# Revit family: WALL SQUARE 6W ASIMETRICA_LKC0635A_WW
name_source: partatom
category: Luminarias
units: mm (PartAtom-declared; Revit-internal decimal feet)

## family parameters
Compartido = No
Corte con vacíos al cargar = No
Cota de conector redondo = Diámetro de uso
Origen de luz = Sí
Punto de cálculo de habitación = No
Se basa en plano de trabajo = Sí
Siempre vertical = No
Tipo de pieza = Normal

## types (2) — shared parameters
Ancho = 160 mm  [stored 0.524934 ft]
Cambio de temperatura de color de luz atenuada = <Ninguno>
Comentarios de vataje = 100-240V
Fabricante = BRILLANT
Filtro de color = 16777215
Longitud de símbolo de origen de luz = 500 mm  [stored 1.64042 ft]
Lámpara = OSRAM
Watt per fixture = 6
Ángulo de campo de foco = 45.00°
Ángulo de enfoque = 35.00°
Ángulo de inclinación = 105.00°
zero-valued in all types: Elevación por defecto

## per-type parameters (varying)
| type | Descripción | Modelo |
| EMP_LKC0635A | LUMINARIA TIPO CUADRADO PARA EMPOTRAR EN PISO CON CUERPO DE ALUMINIO FUNDIDO A PRESION, CUBIERTO CON POLVO GRIS OSCURO CON CUBIERTA DE ACERO INOXIDABLE Y VIDRIO TEMPLADO DE 8MM, HOUSING DE METAL 1.5MM CUBIERTO DE POLVO GRIS OSCURO DE 160MM Y 118MM DE PROFUNDO CON PESO DE 2.5KG. CUENTA CON 6 LED TIPO OSRAM CON UNA POTENCIA TOTAL DE 6W, TEMPERATURA EN BLANCO ULTRA CALIDO EN 2000K CON 247 LUMENES, IP67, IK09, IRC 80 APERTURA ASIMETRICA DE 45X35 GRADOS POR STOCK, ALIMENTADA A 100-240V. | LKC0635A |
| EMP_LKC0635WW | LUMINARIA TIPO CUADRADO PARA EMPOTRAR EN PISO CON CUERPO DE ALUMINIO FUNDIDO A PRESION, CUBIERTO CON POLVO GRIS OSCURO CON CUBIERTA DE ACERO INOXIDABLE Y VIDRIO TEMPLADO DE 8MM, HOUSING DE METAL 1.5MM CUBIERTO DE POLVO GRIS OSCURO DE 160MM Y 118MM DE PROFUNDO CON PESO DE 2.5KG. CUENTA CON 6 LED TIPO OSRAM CON UNA POTENCIA TOTAL DE 6W, TEMPERATURA EN BLANCO CALIDO EN 3000K CON 247 LUMENES, IP67, IK09, IRC 80 APERTURA ASIMETRICA DE 45X35 GRADOS POR STOCK, ALIMENTADA A 100-240V. | LKC0635WW |

note: [stored X ft] marks values corroborated as IEEE doubles in the binary element streams (Revit-internal decimal feet)

## geometry (parser evidence)
native form markers: Blend x2
no freeform markers — native parametric forms only
